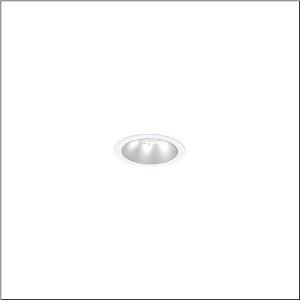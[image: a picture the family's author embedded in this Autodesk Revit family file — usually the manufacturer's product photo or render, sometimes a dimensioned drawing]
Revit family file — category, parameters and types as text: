
# Revit family: lunis_21_s_51db19ma91c
name_source: partatom
category: Lighting Fixtures
units: mm (PartAtom-declared; Revit-internal decimal feet)

## family parameters
Cut with Voids When Loaded = No
Host = Face
Light Source = No
Part Type = Normal
Room Calculation Point = No
Round Connector Dimension = Use Diameter
Shared = No

## types (1)
- --- (1 x LED, 930 lm, 5.9 W, 6500K)
    Apparent Load = 6 VA
    CIE Flux Codes = 90 98 100 100 100
    Color Rendering = 80
    Color Temperature = 6500K
    Default Elevation = 1800 mm
    Description = Lunis 21,  S, downlight, light control with lens, of PMMA, anti glare with reflector, of PC, matt, light emission: direct distribution, LED rated luminous flux: 940lm, light colour: 830/840/865, with terminal, 3-pole, mains connection: 220..240V, AC, 50..60Hz, housing, round, of diecast aluminium, traffic white (RAL 9016), diameter: 84mm, clamping range: 1..40mm, protection rating (complete): IP20, protection rating (on room side): IP54, insulation class (complete): insulation class II (safety insulation), certification: CE, impact resistance: IK03, packaging unit: 1 piece
    Height = 0 mm  [stored 0 ft]
    Lamp = 1 x LED
    Lamp Light Flux = 930 lm
    Lamp Power = 5.9 W
    Lamp count = 1
    Length = 84 mm
    Luminous efficacy = 158 lm/W
    Manufacturer = Siteco
    ModVariant = No
    Model = 51DB19MA91C
    Mounting Place = Ceiling
    Mounting Type = Recessed
    Number of Poles = 1
    OnlyDefault = Yes
    Power Factor = 1
    Product Name = Lunis 21 S
    Product group = downlight
    ProductGroupID = 400
    Protection Class = Protection class II
    Protection Degree = IP 20
    RLX_Detail_Level = 1
    RLX_Emergency_Light_Flux = 0 lm
    RLX_Emergency_Type = 0
    RLX_Emergency_Type_DB = No
    RlxData = <blob elided: 8581 chars, md5=ade6c69d>
    Socket = socket
    Standby Power = 0 W
    System Light Flux = 930 lm
    System Power = 6 W
    Type Comments = individual setting: colour temperature 6500K
    Type Image = l_1290846.jpg
    URL = http://relux.com
    VarID = @adj_019202
    Voltage = 0 V
    Weight = 0.00 kg
    Width = 0 mm  [stored 0 ft]

note: [stored X ft] marks values corroborated as IEEE doubles in the binary element streams (Revit-internal decimal feet)

## geometry (parser evidence)
native form markers: Sweep x8
no freeform markers — native parametric forms only
